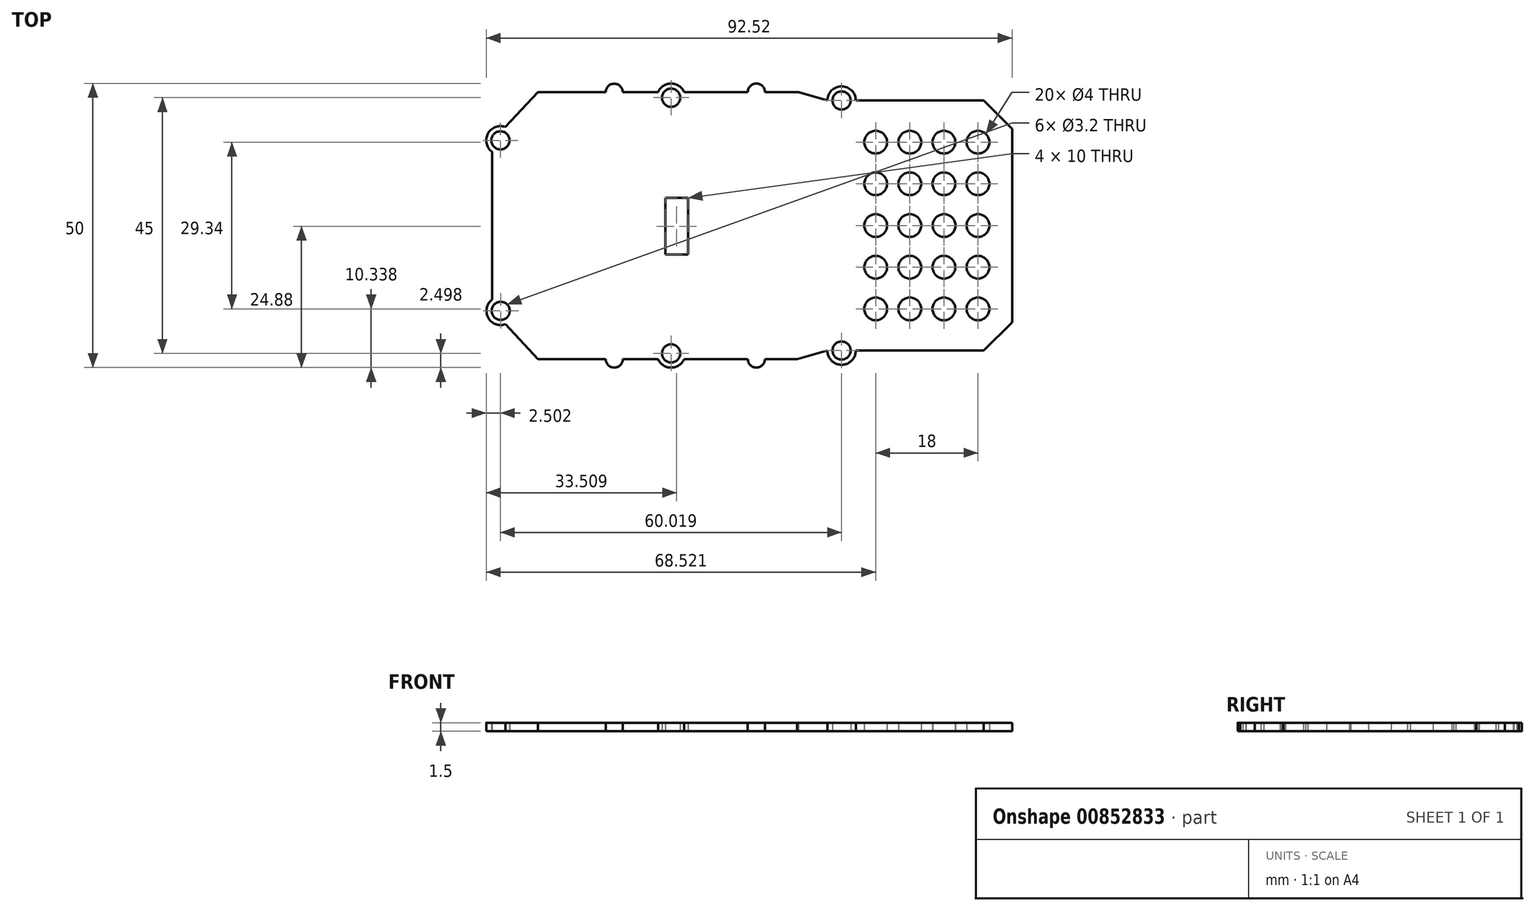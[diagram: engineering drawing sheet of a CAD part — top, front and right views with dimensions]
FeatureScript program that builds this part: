
annotation { "Feature Type Name" : "Feature", "Feature Type Description" : "" }
export const myFeature = defineFeature(function(context is Context, id is Id, definition is map)
    precondition{}
    {
        {
            var Q0;
            Q0=qCreatedBy(makeId("Top.planeOp"),FACE);
            var sketch = newSketch(context, id + "F0", { "sketchPlane" : qUnion([Q0])});
            skPoint(sketch, "E0.middle", {"position": v(11.15, 0.12) * mm});
            skLineSegment(sketch, "E1", {"start": v(-29.35, 22.13) * mm, "end": v(38.65, 22.13) * mm, "construction": true});
            skLineSegment(sketch, "E2", {"start": v(-29.35, -21.88) * mm, "end": v(38.65, -21.88) * mm, "construction": true});
            skLineSegment(sketch, "E3", {"start": v(-29.35, 22.13) * mm, "end": v(-29.35, -21.88) * mm, "construction": true});
            skLineSegment(sketch, "E4", {"start": v(30.84, -23.38) * mm, "end": v(36.15, -21.88) * mm});
            skLineSegment(sketch, "E5", {"start": v(31.09, 23.63) * mm, "end": v(36.15, 22.13) * mm});
            skLineSegment(sketch, "E6", {"start": v(-14.78, 23.62) * mm, "end": v(-2.85, 23.62) * mm});
            skLineSegment(sketch, "E7", {"start": v(-14.77, -23.38) * mm, "end": v(-2.85, -23.38) * mm});
            skCircle(sketch, "E8", {"center": v(38.65, 22.13) * mm, "radius": 1.6 * mm});
            skCircle(sketch, "E9", {"center": v(38.65, -21.88) * mm, "radius": 1.6 * mm});
            skArc(sketch, "E10", {"start": v(0.15, 23.6) * mm, "mid": v(-1.35, 25.1) * mm, "end": v(-2.85, 23.6) * mm});
            skArc(sketch, "E11", {"start": v(22.15, -23.38) * mm, "mid": v(23.65, -24.88) * mm, "end": v(25.15, -23.38) * mm});
            skArc(sketch, "E12", {"start": v(25.15, 23.62) * mm, "mid": v(23.65, 25.12) * mm, "end": v(22.15, 23.62) * mm});
            skArc(sketch, "E13", {"start": v(-2.85, -23.38) * mm, "mid": v(-1.35, -24.88) * mm, "end": v(0.15, -23.38) * mm});
            skCircle(sketch, "E14", {"center": v(8.65, 22.62) * mm, "radius": 1.6 * mm});
            skCircle(sketch, "E15", {"center": v(8.65, -22.38) * mm, "radius": 1.6 * mm});
            skCircle(sketch, "E16", {"center": v(-21.32, -14.9) * mm, "radius": 1.6 * mm});
            skCircle(sketch, "E17", {"center": v(-21.37, 15.12) * mm, "radius": 1.6 * mm});
            skLineSegment(sketch, "E18", {"start": v(10.94, 23.62) * mm, "end": v(10.94, 23.62) * mm});
            skArc(sketch, "E19", {"start": v(36.15, -21.88) * mm, "mid": v(38.66, -24.38) * mm, "end": v(41.15, -21.87) * mm});
            skLineSegment(sketch, "E20", {"start": v(6.36, -23.38) * mm, "end": v(6.36, -23.38) * mm});
            skLineSegment(sketch, "E21", {"start": v(10.94, -23.38) * mm, "end": v(10.94, -23.38) * mm});
            skArc(sketch, "E22", {"start": v(6.36, -23.38) * mm, "mid": v(8.65, -24.88) * mm, "end": v(10.94, -23.38) * mm});
            skLineSegment(sketch, "E23", {"start": v(10.94, -23.38) * mm, "end": v(22.15, -23.38) * mm});
            skLineSegment(sketch, "E24", {"start": v(-2.85, -23.38) * mm, "end": v(-2.85, -23.38) * mm});
            skLineSegment(sketch, "E25", {"start": v(0.15, -23.38) * mm, "end": v(0.15, -23.38) * mm});
            skLineSegment(sketch, "E26", {"start": v(0.15, -23.38) * mm, "end": v(6.36, -23.38) * mm});
            skLineSegment(sketch, "E27", {"start": v(-20.5, -17.26) * mm, "end": v(-20.5, -17.26) * mm});
            skLineSegment(sketch, "E28", {"start": v(-20.5, -17.26) * mm, "end": v(-14.77, -23.38) * mm});
            skArc(sketch, "E29", {"start": v(-22.85, -12.92) * mm, "mid": v(-23.52, -16.09) * mm, "end": v(-20.5, -17.26) * mm});
            skLineSegment(sketch, "E30", {"start": v(-20.52, 17.47) * mm, "end": v(-14.78, 23.62) * mm});
            skArc(sketch, "E31", {"start": v(-20.52, 17.47) * mm, "mid": v(-23.57, 16.3) * mm, "end": v(-22.85, 13.1) * mm});
            skLineSegment(sketch, "E32", {"start": v(-22.85, 13.1) * mm, "end": v(-22.85, -12.92) * mm});
            skLineSegment(sketch, "E33", {"start": v(0.15, 23.62) * mm, "end": v(6.36, 23.62) * mm});
            skLineSegment(sketch, "E34", {"start": v(6.36, 23.62) * mm, "end": v(6.36, 23.62) * mm});
            skLineSegment(sketch, "E35", {"start": v(10.94, 23.62) * mm, "end": v(22.15, 23.62) * mm});
            skArc(sketch, "E36", {"start": v(10.94, 23.62) * mm, "mid": v(8.65, 25.12) * mm, "end": v(6.36, 23.62) * mm});
            skLineSegment(sketch, "E37", {"start": v(25.15, 23.63) * mm, "end": v(31.09, 23.63) * mm});
            skLineSegment(sketch, "E38", {"start": v(22.15, -23.38) * mm, "end": v(22.15, -23.38) * mm});
            skLineSegment(sketch, "E39", {"start": v(25.15, -23.38) * mm, "end": v(25.15, -23.38) * mm});
            skLineSegment(sketch, "E40", {"start": v(25.15, -23.38) * mm, "end": v(30.84, -23.38) * mm});
            skLineSegment(sketch, "E41.bottom", {"start": v(38.65, 22.13) * mm, "end": v(38.65, 22.13) * mm});
            skLineSegment(sketch, "E42", {"start": v(41.15, -21.88) * mm, "end": v(41.15, -21.88) * mm});
            skLineSegment(sketch, "E43", {"start": v(38.78, -19.39) * mm, "end": v(38.78, -19.39) * mm});
            skArc(sketch, "E44", {"start": v(41.15, 22.13) * mm, "mid": v(38.65, 24.63) * mm, "end": v(36.15, 22.13) * mm});
            skLineSegment(sketch, "E45", {"start": v(63.65, 22.13) * mm, "end": v(68.65, 17.12) * mm});
            skLineSegment(sketch, "E46", {"start": v(63.65, -21.87) * mm, "end": v(68.65, -16.88) * mm});
            skLineSegment(sketch, "E47", {"start": v(41.15, 22.13) * mm, "end": v(63.65, 22.13) * mm});
            skLineSegment(sketch, "E48", {"start": v(68.65, 17.12) * mm, "end": v(68.65, -16.88) * mm});
            skLineSegment(sketch, "E49", {"start": v(41.15, -21.87) * mm, "end": v(63.65, -21.87) * mm});
            skCircle(sketch, "E50", {"center": v(44.65, 14.8) * mm, "radius": 2 * mm});
            skCircle(sketch, "E51", {"center": v(50.65, 14.8) * mm, "radius": 2 * mm});
            skCircle(sketch, "E52", {"center": v(56.65, 14.8) * mm, "radius": 2 * mm});
            skCircle(sketch, "E53", {"center": v(62.65, 14.8) * mm, "radius": 2 * mm});
            skCircle(sketch, "E54", {"center": v(44.65, 7.47) * mm, "radius": 2 * mm});
            skCircle(sketch, "E55", {"center": v(50.65, 7.47) * mm, "radius": 2 * mm});
            skCircle(sketch, "E56", {"center": v(56.65, 7.47) * mm, "radius": 2 * mm});
            skCircle(sketch, "E57", {"center": v(62.65, 7.47) * mm, "radius": 2 * mm});
            skCircle(sketch, "E58", {"center": v(44.65, 0.13) * mm, "radius": 2 * mm});
            skCircle(sketch, "E59", {"center": v(50.65, 0.13) * mm, "radius": 2 * mm});
            skCircle(sketch, "E60", {"center": v(56.68, 0.13) * mm, "radius": 2 * mm});
            skCircle(sketch, "E61", {"center": v(62.65, 0.13) * mm, "radius": 2 * mm});
            skCircle(sketch, "E62", {"center": v(44.65, -7.21) * mm, "radius": 2 * mm});
            skCircle(sketch, "E63", {"center": v(50.65, -7.21) * mm, "radius": 2 * mm});
            skCircle(sketch, "E64", {"center": v(56.65, -7.21) * mm, "radius": 2 * mm});
            skCircle(sketch, "E65", {"center": v(62.65, -7.21) * mm, "radius": 2 * mm});
            skCircle(sketch, "E66", {"center": v(44.65, -14.54) * mm, "radius": 2 * mm});
            skCircle(sketch, "E67", {"center": v(50.65, -14.54) * mm, "radius": 2 * mm});
            skCircle(sketch, "E68", {"center": v(56.65, -14.54) * mm, "radius": 2 * mm});
            skCircle(sketch, "E69", {"center": v(62.65, -14.54) * mm, "radius": 2 * mm});
            skLineSegment(sketch, "E70", {"start": v(8.65, 22.62) * mm, "end": v(8.65, -22.38) * mm, "construction": true});
            skLineSegment(sketch, "E71.bottom", {"start": v(11.64, 5) * mm, "end": v(7.64, 5) * mm});
            skLineSegment(sketch, "E71.top", {"start": v(11.64, -5) * mm, "end": v(7.64, -5) * mm});
            skLineSegment(sketch, "E71.left", {"start": v(11.64, 5) * mm, "end": v(11.64, -5) * mm});
            skLineSegment(sketch, "E71.right", {"start": v(7.64, 5) * mm, "end": v(7.64, -5) * mm});
            skPoint(sketch, "E71.middle", {"position": v(9.64, 0) * mm});
            skSolve(sketch);
        }
        {
            var Q0;
            Q0=makeQuery(id+"F0.imprint","IMPRINT",FACE,{"disambiguationData":[TD([[makeQuery(id+"F0.imprint","IMPRINT",EDGE,{"derivedFrom":sQuery(id+"F0.wireOp",EDGE,"E4")}),1.0]])]});
            extrude(context, id + "F1", {"entities" : qUnion([Q0]), "depth" : 1.5 * mm, "offsetDistance" : 25 * mm});
        }
    });
